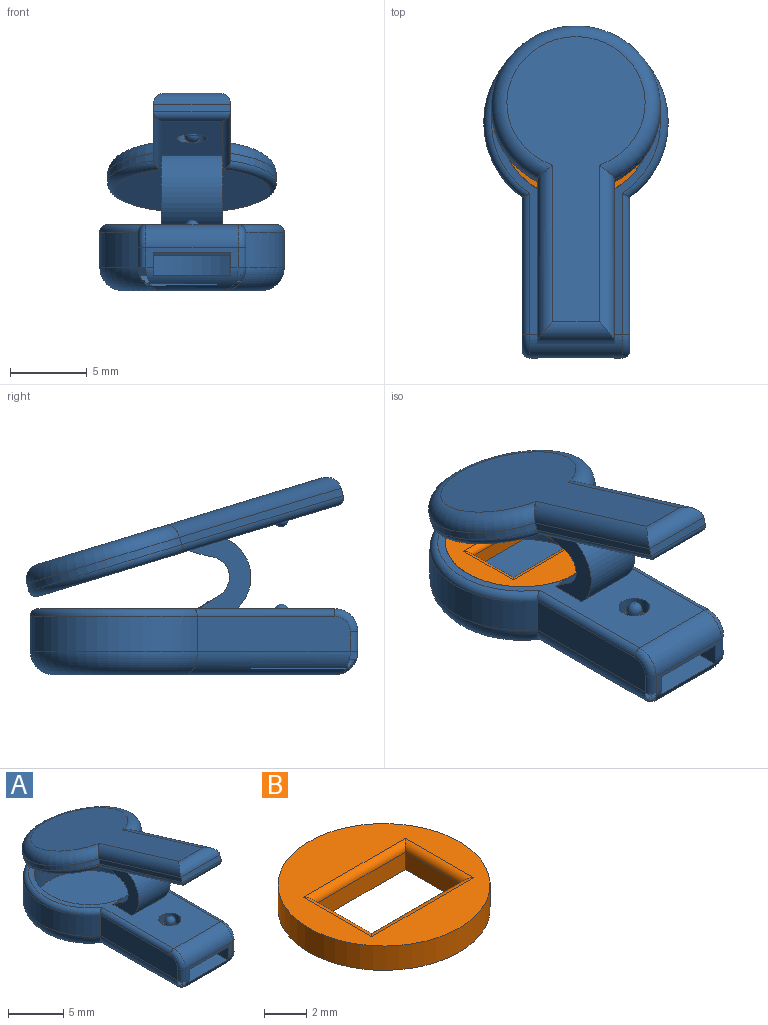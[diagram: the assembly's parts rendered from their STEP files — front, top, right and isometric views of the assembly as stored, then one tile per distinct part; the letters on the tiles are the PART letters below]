
ASSEMBLY  parts=2 mates=1
PART A: 55 faces, bbox 13.8x23x13.9 mm
  f0: plane 8.09x4.82mm, normal (0,-0.29,-0.96), area 27.1mm2, adj f35,f36,f38,f43,f51
  f1: plane 10x9.77mm, normal (0,-0.29,-0.96), area 80mm2, adj f35,f37,f38,f46
  f2: plane 11x1.5mm, normal (-1,0,0), area 14.4mm2, adj f4,f5,f11,f12,f16,f27
  f3: plane 11x1.5mm, normal (1,0,0), area 14.4mm2, adj f4,f5,f11,f12,f16,f27
  f4: plane 6x1.3mm, normal (0,-1,0), area 2.8mm2, adj f2,f3,f5,f17,f19,f25,f27
  f5: cylinder r=1.5mm len=6mm, axis (-1,0,0), area 9.2mm2, adj f2,f3,f4,f10,f12,f18,f26
  f6: plane 19.62x11.29mm, normal (0,0,1), area 55.2mm2, adj f11,f17,f21,f22,f23,f28,f29,f43
  f7: plane 9.96x2.3mm, normal (1,0,0), area 22.7mm2, adj f8,f15,f23,f24,f25
  f8: cylinder r=6mm len=12mm, axis (0,0,1), area 69.5mm2, adj f7,f9,f13,f22
  f9: plane 9.96x2.3mm, normal (-1,0,0), area 22.7mm2, adj f8,f14,f19,f20,f21
  f10: plane 18.33x9mm, normal (0,0,-1), area 101.5mm2, adj f5,f13,f14,f15
  f11: cylinder r=5mm len=10mm, axis (0,0,1), area 96.9mm2, adj f2,f3,f6,f12,f16,f45
  f12: plane 20.24x10mm, normal (0,0,1), area 130.8mm2, adj f2,f3,f5,f11
  f13: torus R=4.5mm, axis (0,0,1), area 66.7mm2, adj f8,f10,f14,f15
  f14: cylinder r=1.5mm len=10.8mm, axis (0,1,0), area 23.3mm2, adj f9,f10,f13,f18
  f15: cylinder r=1.5mm len=10.8mm, axis (0,-1,0), area 23.3mm2, adj f7,f10,f13,f26
  f16: plane 9.5x5mm, normal (0,0,-1), area 45.2mm2, adj f2,f3,f11,f27
  f17: cylinder r=1.5mm len=6mm, axis (1,0,0), area 14.1mm2, adj f4,f6,f20,f24
  f18: bspline ~1.76x1.5mm, area 0.8mm2, adj f5,f14,f19
  f19: cylinder r=0.5mm len=1.3mm, axis (0,0,1), area 1mm2, adj f4,f9,f18,f20
  f20: torus R=1mm, axis (-1,0,0), area 1.6mm2, adj f9,f17,f19,f21
  f21: cylinder r=0.5mm len=9.22mm, axis (0,-1,0), area 7.1mm2, adj f6,f9,f20,f22
  f22: torus R=5.5mm, axis (0,0,1), area 23.2mm2, adj f6,f8,f21,f23
  f23: cylinder r=0.5mm len=9.22mm, axis (0,1,0), area 7.1mm2, adj f6,f7,f22,f24
  f24: torus R=1mm, axis (-1,0,0), area 1.6mm2, adj f7,f17,f23,f25
  f25: cylinder r=0.5mm len=1.3mm, axis (0,0,-1), area 1mm2, adj f4,f7,f24,f26
  f26: bspline ~1.57x1.5mm, area 0.8mm2, adj f5,f15,f25
  f27: plane 5x1.5mm, normal (0,-0.13,-0.99), area 7.6mm2, adj f2,f3,f4,f16
  f28: plane 4.6x4.13mm, normal (-1,0,0), area 8.3mm2, adj f6,f35,f43,f44,f45,f46
  f29: plane 4.6x4.13mm, normal (1,0,0), area 8.3mm2, adj f6,f38,f43,f44,f45,f46
  f30: cylinder r=5.5mm len=11mm, axis (0,-0.29,-0.96), area 14.7mm2, adj f31,f33,f37,f41
  f31: plane 10.67x3.68mm, normal (1,0,0), area 5.5mm2, adj f30,f32,f38,f42
  f32: plane 5x0.48mm, normal (0,-0.96,0.29), area 2.5mm2, adj f31,f33,f36,f40
  f33: plane 10.67x3.68mm, normal (-1,0,0), area 5.5mm2, adj f30,f32,f35,f39
  f34: plane 18.56x9mm, normal (0,0.29,0.96), area 95.1mm2, adj f39,f40,f41,f42
  f35: cylinder r=0.5mm len=10.97mm, axis (0,0.96,-0.29), area 8.6mm2, adj f0,f1,f28,f33,f36,f37
  f36: cylinder r=0.5mm len=5mm, axis (-1,0,0), area 3.5mm2, adj f0,f32,f35,f38
  f37: torus R=5mm, axis (0,-0.29,-0.96), area 22.6mm2, adj f1,f30,f35,f38
  f38: cylinder r=0.5mm len=10.97mm, axis (0,-0.96,0.29), area 8.6mm2, adj f0,f1,f29,f31,f36,f37
  f39: cylinder r=1mm len=11.44mm, axis (0,-0.96,0.29), area 17mm2, adj f33,f34,f40,f41
  f40: cylinder r=1mm len=5mm, axis (1,0,0), area 6.3mm2, adj f32,f34,f39,f42
  f41: torus R=4.5mm, axis (0,-0.29,-0.96), area 44.1mm2, adj f30,f34,f39,f42
  f42: cylinder r=1mm len=11.44mm, axis (0,0.96,-0.29), area 17mm2, adj f31,f34,f40,f41
  f43: cylinder r=2.75mm len=4.53mm, axis (-1,0,0), area 21.7mm2, adj f0,f6,f28,f29
  f44: cylinder r=1.35mm len=4mm, axis (-1,0,0), area 13.2mm2, adj f28,f29,f45,f46
  f45: bspline ~5.2x2.06mm, area 6.2mm2, adj f6,f11,f28,f29,f44
  f46: cylinder r=10mm len=4mm, axis (1,0,0), area 6.5mm2, adj f1,f28,f29,f44
  f47: cylinder r=0.5mm len=1mm, axis (0,0,1), area 2.5mm2, adj f48,f54
  f48: plane 2x2mm, normal (0,0,1), area 2.4mm2, adj f47,f49
  f49: cylinder r=1mm len=2mm, axis (0,0,1), area 6.3mm2, adj f6,f48
  f50: cylinder r=0.5mm len=1mm, axis (0,0,1), area 2.1mm2, adj f52,f53
  f51: cylinder r=1mm len=2mm, axis (0,0,1), area 4.6mm2, adj f0,f52
  f52: plane 2x2mm, normal (0,0,-1), area 2.4mm2, adj f50,f51
  f53: sphere r=0.5mm, area 1.8mm2, adj f50
  f54: sphere r=0.5mm, area 1.6mm2, adj f47
PART B: 11 faces, bbox 10x10x1.4 mm
  f0: plane 3.75x1mm, normal (1,0,0), area 3.8mm2, adj f1,f4,f5,f7
  f1: plane 6x1mm, normal (0,-1,0), area 6mm2, adj f0,f2,f5,f8
  f2: plane 3.75x1mm, normal (-1,0,0), area 3.8mm2, adj f1,f4,f5,f10
  f3: cylinder r=5mm len=10mm, axis (0,0,1), area 44mm2, adj f5,f6
  f4: plane 6x1mm, normal (0,1,0), area 6mm2, adj f0,f2,f5,f9
  f5: plane 10x10mm, normal (0,0,-1), area 56mm2, adj f0,f1,f2,f3,f4
  f6: plane 10x10mm, normal (0,0,1), area 47.6mm2, adj f3,f7,f8,f9,f10
  f7: cylinder r=0.4mm len=4.55mm, axis (0,1,0), area 2.5mm2, adj f0,f6,f8,f9
  f8: cylinder r=0.4mm len=6.8mm, axis (1,0,0), area 4mm2, adj f1,f6,f7,f10
  f9: cylinder r=0.4mm len=6.8mm, axis (-1,0,0), area 4mm2, adj f4,f6,f7,f10
  f10: cylinder r=0.4mm len=4.55mm, axis (0,-1,0), area 2.5mm2, adj f2,f6,f8,f9
PLACE A t=(18.01,-1.36,0.15)mm
PLACE B t=(18.01,-1.36,0.15)mm
MATE slider B.f3 <-> A.f8  axis (0,0,1) through (18.01,-1.36,0.15)mm
